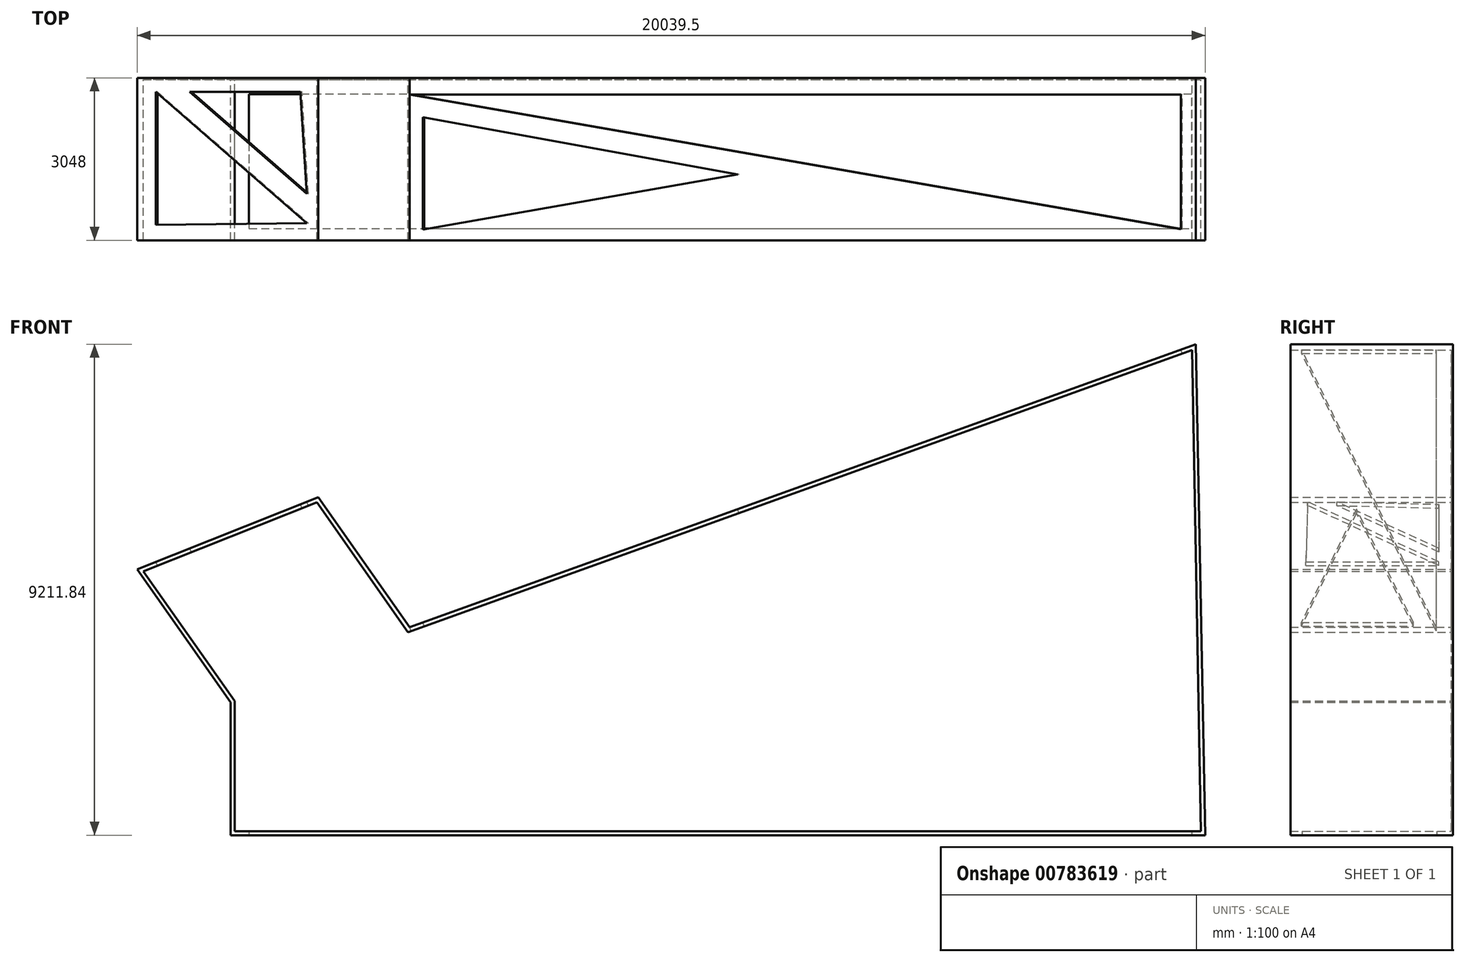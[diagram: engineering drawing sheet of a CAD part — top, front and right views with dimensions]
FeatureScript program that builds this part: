
annotation { "Feature Type Name" : "Feature", "Feature Type Description" : "" }
export const myFeature = defineFeature(function(context is Context, id is Id, definition is map)
    precondition{}
    {
        {
            var Q0;
            Q0=qCreatedBy(makeId("Front.planeOp"),FACE);
            var sketch = newSketch(context, id + "F0", { "sketchPlane" : qUnion([Q0])});
            skLineSegment(sketch, "E0", {"start": v(-8880.46, 0) * mm, "end": v(9407.54, 0) * mm});
            skLineSegment(sketch, "E1", {"start": v(-8880.46, 0) * mm, "end": v(-8880.46, 2493.43) * mm});
            skLineSegment(sketch, "E2", {"start": v(-8880.46, 2493.43) * mm, "end": v(-10631.92, 4987.96) * mm});
            skLineSegment(sketch, "E3", {"start": v(-10631.92, 4987.96) * mm, "end": v(-7233.6, 6340.55) * mm});
            skLineSegment(sketch, "E4", {"start": v(-7233.6, 6340.55) * mm, "end": v(-5521.34, 3901.84) * mm});
            skLineSegment(sketch, "E5", {"start": v(-5521.34, 3901.84) * mm, "end": v(9233.8, 9211.84) * mm});
            skLineSegment(sketch, "E6", {"start": v(9233.8, 9211.84) * mm, "end": v(9407.54, 0) * mm});
            skLineSegment(sketch, "E7.0", {"start": v(-8804.26, 76.2) * mm, "end": v(-8804.26, 2517.5) * mm});
            skLineSegment(sketch, "E7.1", {"start": v(-8804.26, 2517.5) * mm, "end": v(-10514.14, 4952.82) * mm});
            skLineSegment(sketch, "E7.2", {"start": v(9159.62, 9104.16) * mm, "end": v(9329.89, 76.2) * mm});
            skLineSegment(sketch, "E7.4", {"start": v(-7261.37, 6247.48) * mm, "end": v(-5550.28, 3810.44) * mm});
            skLineSegment(sketch, "E7.5", {"start": v(-8804.26, 76.2) * mm, "end": v(9329.89, 76.2) * mm});
            skLineSegment(sketch, "E7.6", {"start": v(-10514.14, 4952.82) * mm, "end": v(-7261.37, 6247.48) * mm});
            skLineSegment(sketch, "E8", {"start": v(-5550.28, 3810.44) * mm, "end": v(9159.62, 9104.16) * mm});
            skSolve(sketch);
        }
        {
            var Q0;
            Q0=makeQuery(id+"F0.imprint","IMPRINT",FACE,{"disambiguationData":[TD([[makeQuery(id+"F0.imprint","IMPRINT",EDGE,{"derivedFrom":sQuery(id+"F0.wireOp",EDGE,"E0")}),1.0]])]});
            extrude(context, id + "F1", {"entities" : qUnion([Q0]), "depth" : 3048 * mm, "offsetDistance" : 30.48 * mm});
        }
        {
            var Q0;
            Q0=makeQuery(id+"F0.imprint","IMPRINT",FACE,{"disambiguationData":[TD([[makeQuery(id+"F0.imprint","IMPRINT",EDGE,{"derivedFrom":sQuery(id+"F0.wireOp",EDGE,"E7.0")}),-1.0]])]});
            extrude(context, id + "F2", {"entities" : qUnion([Q0]), "operationType" : NewBodyOperationType.ADD, "depth" : 30.48 * mm, "offsetDistance" : 30.48 * mm});
        }
        {
            var Q0;
            Q0=makeQuery(id+"F1.opExtrude","SWEPT_FACE",FACE,{"disambiguationData":[OSD([sQuery(id+"F0.wireOp",EDGE,"E0")])]});
            var sketch = newSketch(context, id + "F3", { "sketchPlane" : qUnion([Q0])});
            skLineSegment(sketch, "E9", {"start": v(-8533.06, 2826.13) * mm, "end": v(9154.07, 2826.13) * mm});
            skLineSegment(sketch, "E10", {"start": v(9154.07, 2826.13) * mm, "end": v(9154.07, 303.59) * mm});
            skLineSegment(sketch, "E11", {"start": v(9154.07, 303.59) * mm, "end": v(-8533.06, 303.59) * mm});
            skLineSegment(sketch, "E12", {"start": v(-8533.06, 303.59) * mm, "end": v(-8533.06, 2826.13) * mm});
            skSolve(sketch);
        }
        {
            var Q0;
            Q0=makeQuery(id+"F3.imprint","IMPRINT",FACE,{"disambiguationData":[TD([[makeQuery(id+"F3.imprint","IMPRINT",EDGE,{"derivedFrom":sQuery(id+"F3.wireOp",EDGE,"E9")}),-1.0]])]});
            extrude(context, id + "F4", {"entities" : qUnion([Q0]), "operationType" : NewBodyOperationType.REMOVE, "oppositeDirection" : true, "depth" : 76.2 * mm, "offsetDistance" : 30.48 * mm});
        }
        {
            var Q0;
            Q0=makeQuery(id+"F1.opExtrude","SWEPT_FACE",FACE,{"disambiguationData":[OSD([sQuery(id+"F0.wireOp",EDGE,"E5")])]});
            var sketch = newSketch(context, id + "F5", { "sketchPlane" : qUnion([Q0])});
            skLineSegment(sketch, "E13", {"start": v(11510.63, -2836.42) * mm, "end": v(11510.63, -313.8) * mm});
            skLineSegment(sketch, "E14", {"start": v(11510.63, -313.8) * mm, "end": v(-3873.95, -313.8) * mm});
            skLineSegment(sketch, "E15", {"start": v(-3873.95, -313.8) * mm, "end": v(11510.63, -2836.42) * mm});
            skSolve(sketch);
        }
        {
            var Q0;
            Q0=makeQuery(id+"F5.imprint","IMPRINT",FACE,{"disambiguationData":[TD([[makeQuery(id+"F5.imprint","IMPRINT",EDGE,{"derivedFrom":sQuery(id+"F5.wireOp",EDGE,"E13")}),1.0]])]});
            extrude(context, id + "F6", {"entities" : qUnion([Q0]), "operationType" : NewBodyOperationType.REMOVE, "oppositeDirection" : true, "depth" : 76.2 * mm, "offsetDistance" : 30.48 * mm});
        }
        {
            var Q0;
            Q0=makeQuery(id+"F1.opExtrude","SWEPT_FACE",FACE,{"disambiguationData":[OSD([sQuery(id+"F0.wireOp",EDGE,"E5")])]});
            var sketch = newSketch(context, id + "F7", { "sketchPlane" : qUnion([Q0])});
            skLineSegment(sketch, "E16", {"start": v(-3606.99, -2843.41) * mm, "end": v(-3606.99, -739.27) * mm});
            skLineSegment(sketch, "E17", {"start": v(-3606.99, -739.27) * mm, "end": v(2668.94, -1808.3) * mm});
            skLineSegment(sketch, "E18", {"start": v(2668.94, -1808.3) * mm, "end": v(-3606.99, -2843.41) * mm});
            skSolve(sketch);
        }
        {
            var Q0;
            Q0 = qSketchRegion(id + "F7", true);
            extrude(context, id + "F8", {"entities" : qUnion([Q0]), "operationType" : NewBodyOperationType.REMOVE, "oppositeDirection" : true, "depth" : 76.2 * mm, "offsetDistance" : 30.48 * mm});
        }
        {
            var Q0;
            Q0=makeQuery(id+"F1.opExtrude","SWEPT_FACE",FACE,{"disambiguationData":[OSD([sQuery(id+"F0.wireOp",EDGE,"E3")])]});
            var sketch = newSketch(context, id + "F9", { "sketchPlane" : qUnion([Q0])});
            skLineSegment(sketch, "E19", {"start": v(-7654.53, -2758.57) * mm, "end": v(-7654.53, -264.14) * mm});
            skLineSegment(sketch, "E20", {"start": v(-7654.53, -264.14) * mm, "end": v(-4606.12, -2724.63) * mm});
            skLineSegment(sketch, "E21", {"start": v(-4606.12, -2724.63) * mm, "end": v(-7654.53, -2758.57) * mm});
            skLineSegment(sketch, "E22", {"start": v(-4606.12, -264.14) * mm, "end": v(-6970.95, -264.14) * mm});
            skLineSegment(sketch, "E23", {"start": v(-6970.95, -264.14) * mm, "end": v(-4606.12, -2172.88) * mm});
            skLineSegment(sketch, "E24", {"start": v(-4606.12, -2172.88) * mm, "end": v(-4735.45, -264.14) * mm});
            skSolve(sketch);
        }
        {
            var Q0;
            {var subQ0=sQuery(id+"F9.wireOp",EDGE,"E23");Q0=makeQuery(id+"F9.imprint","IMPRINT",FACE,{"disambiguationData":[TD([[makeQuery(id+"F9.imprint","IMPRINT",EDGE,{"derivedFrom":subQ0}),1.0]])]});}
            var Q1;
            Q1=makeQuery(id+"F9.imprint","IMPRINT",FACE,{"disambiguationData":[TD([[makeQuery(id+"F9.imprint","IMPRINT",EDGE,{"derivedFrom":sQuery(id+"F9.wireOp",EDGE,"E19")}),-1.0]])]});
            extrude(context, id + "F10", {"entities" : qUnion([Q0, Q1]), "operationType" : NewBodyOperationType.REMOVE, "oppositeDirection" : true, "depth" : 76.2 * mm, "offsetDistance" : 30.48 * mm});
        }
    });
